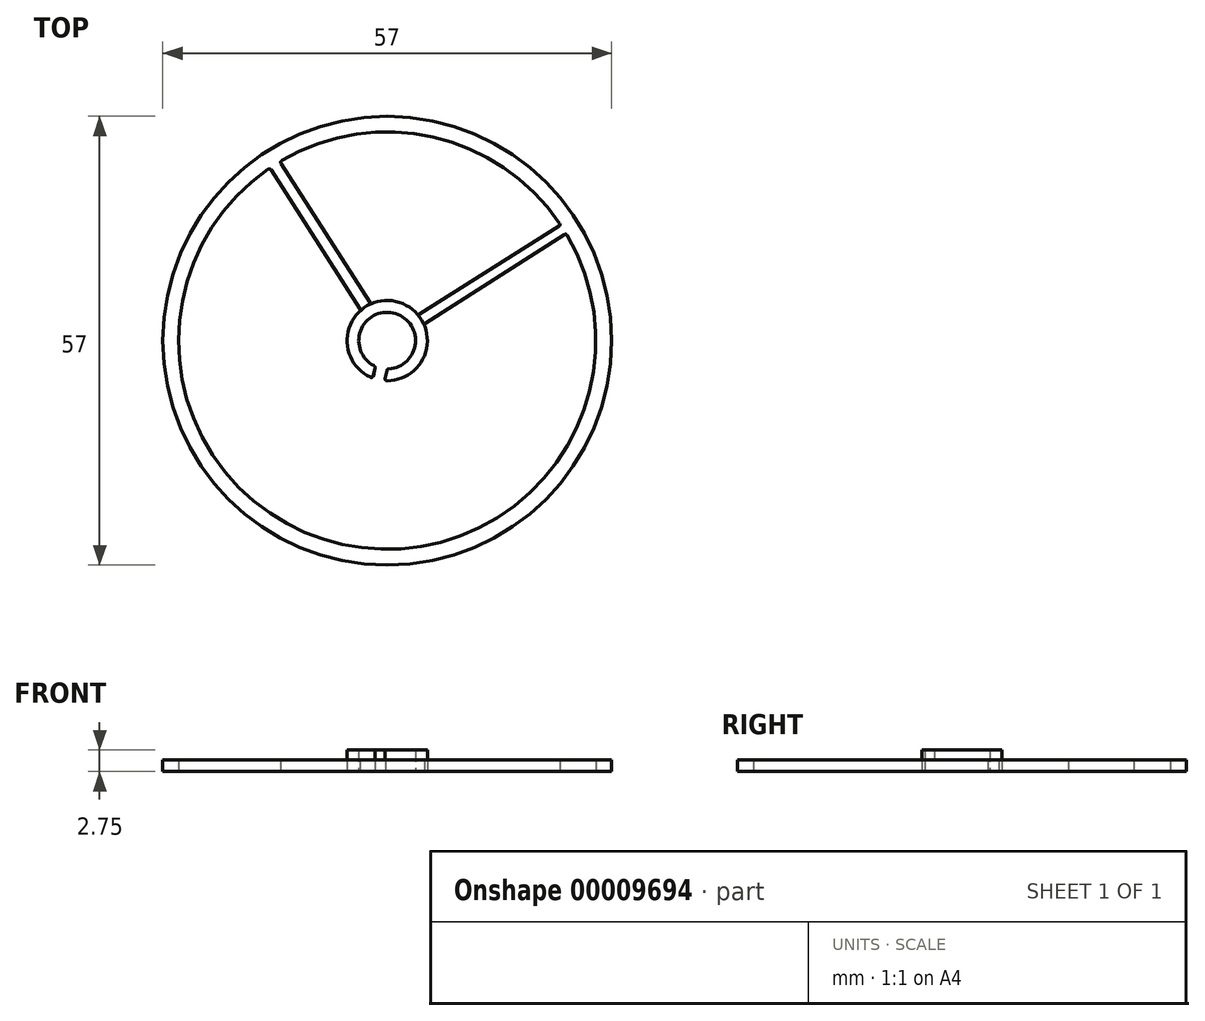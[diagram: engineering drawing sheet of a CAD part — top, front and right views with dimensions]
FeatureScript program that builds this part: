
annotation { "Feature Type Name" : "Feature", "Feature Type Description" : "" }
export const myFeature = defineFeature(function(context is Context, id is Id, definition is map)
    precondition{}
    {
        {
            var Q0;
            Q0=qCreatedBy(makeId("Top.planeOp"),FACE);
            var sketch = newSketch(context, id + "F0", { "sketchPlane" : qUnion([Q0])});
            skCircle(sketch, "E0", {"center": v(0, 0) * mm, "radius": 28.5 * mm});
            skArc(sketch, "E1.0", {"start": v(21.92, 14.89) * mm, "mid": v(5.84, 25.85) * mm, "end": v(-13.4, 22.87) * mm});
            skArc(sketch, "E2", {"start": v(0.2, -3.6) * mm, "mid": v(3.57, -0.47) * mm, "end": v(1.11, 3.42) * mm});
            skArc(sketch, "E3.0", {"start": v(3.8, 3.4) * mm, "mid": v(3.05, 4.08) * mm, "end": v(2.2, 4.6) * mm});
            skLineSegment(sketch, "E4.trimOffspring", {"start": v(4.12, 3.36) * mm, "end": v(21.85, 14.54) * mm});
            skLineSegment(sketch, "E5.trimOffspring", {"start": v(4.84, 2.18) * mm, "end": v(22.52, 13.48) * mm});
            skLineSegment(sketch, "E6.trimOffspring", {"start": v(-2.18, 4.84) * mm, "end": v(-13.48, 22.52) * mm});
            skLineSegment(sketch, "E7.trimOffspring", {"start": v(-3.47, 4.02) * mm, "end": v(-14.74, 21.7) * mm});
            skArc(sketch, "E8.trimOffspring", {"start": v(3.51, -3.7) * mm, "mid": v(4.98, -1.1) * mm, "end": v(4.74, 1.87) * mm});
            skArc(sketch, "E9.trimOffspring", {"start": v(-3.7, -3.51) * mm, "mid": v(-2.95, -4.16) * mm, "end": v(-2.1, -4.65) * mm});
            skArc(sketch, "E10.trimOffspring", {"start": v(-3.5, 3.7) * mm, "mid": v(-5.1, 0.14) * mm, "end": v(-3.7, -3.51) * mm});
            skArc(sketch, "E11.trimOffspring", {"start": v(13.41, -22.85) * mm, "mid": v(25.64, -6.69) * mm, "end": v(22.87, 13.4) * mm});
            skArc(sketch, "E12.trimOffspring", {"start": v(-22.87, -13.4) * mm, "mid": v(-6.69, -25.64) * mm, "end": v(13.41, -22.85) * mm});
            skArc(sketch, "E13.trimOffspring", {"start": v(-15.1, 21.78) * mm, "mid": v(-25.88, 5.72) * mm, "end": v(-22.87, -13.4) * mm});
            skLineSegment(sketch, "E14.0", {"start": v(-1.55, -3.45) * mm, "end": v(-1.75, -4.47) * mm});
            skLineSegment(sketch, "E15.0.MirrorCS", {"start": v(-0.04, -3.8) * mm, "end": v(-0.23, -4.8) * mm});
            skArc(sketch, "E16.trimOffspring", {"start": v(0.02, -5.1) * mm, "mid": v(1.9, -4.73) * mm, "end": v(3.51, -3.7) * mm});
            skArc(sketch, "E17.trimOffspring", {"start": v(1.11, 3.42) * mm, "mid": v(-3.32, 1.4) * mm, "end": v(-1.68, -3.18) * mm});
            skArc(sketch, "E18.trimOffspring", {"start": v(2.2, 4.6) * mm, "mid": v(0.17, 5.1) * mm, "end": v(-1.87, 4.74) * mm});
            skPoint(sketch, "E19.visualSharp", {"position": v(-1.52, -3.26) * mm});
            skArc(sketch, "E19.filletArc", {"start": v(-1.55, -3.45) * mm, "mid": v(-1.57, -3.3) * mm, "end": v(-1.68, -3.18) * mm});
            skPoint(sketch, "E20.visualSharp", {"position": v(-1.8, -4.77) * mm});
            skArc(sketch, "E20.filletArc", {"start": v(-2.1, -4.65) * mm, "mid": v(-1.88, -4.64) * mm, "end": v(-1.75, -4.47) * mm});
            skPoint(sketch, "E21.visualSharp", {"position": v(-0.29, -5.1) * mm});
            skArc(sketch, "E21.filletArc", {"start": v(-0.23, -4.8) * mm, "mid": v(-0.18, -5) * mm, "end": v(0.02, -5.1) * mm});
            skPoint(sketch, "E22.visualSharp", {"position": v(0, -3.6) * mm});
            skArc(sketch, "E22.filletArc", {"start": v(0.2, -3.6) * mm, "mid": v(0.04, -3.66) * mm, "end": v(-0.04, -3.8) * mm});
            skPoint(sketch, "E23.visualSharp", {"position": v(-3.35, 3.84) * mm});
            skArc(sketch, "E23.filletArc", {"start": v(-3.5, 3.7) * mm, "mid": v(-3.43, 3.86) * mm, "end": v(-3.47, 4.02) * mm});
            skPoint(sketch, "E24.visualSharp", {"position": v(-2.06, 4.66) * mm});
            skArc(sketch, "E24.filletArc", {"start": v(-2.18, 4.84) * mm, "mid": v(-2.04, 4.74) * mm, "end": v(-1.87, 4.74) * mm});
            skPoint(sketch, "E25.visualSharp", {"position": v(3.93, 3.24) * mm});
            skArc(sketch, "E25.filletArc", {"start": v(3.8, 3.4) * mm, "mid": v(3.95, 3.32) * mm, "end": v(4.12, 3.36) * mm});
            skPoint(sketch, "E26.visualSharp", {"position": v(4.66, 2.06) * mm});
            skArc(sketch, "E26.filletArc", {"start": v(4.84, 2.18) * mm, "mid": v(4.74, 2.04) * mm, "end": v(4.74, 1.87) * mm});
            skArc(sketch, "E27.filletArc", {"start": v(22.87, 13.4) * mm, "mid": v(22.7, 13.51) * mm, "end": v(22.52, 13.48) * mm});
            skPoint(sketch, "E28.visualSharp", {"position": v(22.07, 14.67) * mm});
            skArc(sketch, "E28.filletArc", {"start": v(21.85, 14.54) * mm, "mid": v(21.96, 14.7) * mm, "end": v(21.92, 14.89) * mm});
            skArc(sketch, "E29.filletArc", {"start": v(-13.4, 22.87) * mm, "mid": v(-13.51, 22.7) * mm, "end": v(-13.48, 22.52) * mm});
            skArc(sketch, "E30.filletArc", {"start": v(-14.74, 21.7) * mm, "mid": v(-14.9, 21.82) * mm, "end": v(-15.1, 21.78) * mm});
            skSolve(sketch);
        }
        {
            var Q0;
            Q0=qSketchRegion(id+"F0",true);
            extrude(context, id + "F1", {"entities" : qUnion([Q0]), "depth" : 1.5 * mm});
        }
        {
            var Q0;
            Q0=makeQuery(id+"F1.opExtrude","CAP_FACE",FACE,{"disambiguationData":[OSD([sQuery(id+"F0.wireOp",EDGE,"E0"),sQuery(id+"F0.wireOp",EDGE,"E1.0"),sQuery(id+"F0.wireOp",EDGE,"E2"),sQuery(id+"F0.wireOp",EDGE,"E3.0"),sQuery(id+"F0.wireOp",EDGE,"9aa386a5-fe43-4538-9e74-4b5fec4a8f2f.0"),sQuery(id+"F0.wireOp",EDGE,"af6841e1-3135-4da6-87f9-270789899b2d.0.MirrorCS"),sQuery(id+"F0.wireOp",EDGE,"af96ccba-543d-44e2-a15b-5b69eeccdc49.0"),sQuery(id+"F0.wireOp",EDGE,"de95141b-281c-47d2-a527-d31a5b29fca6.0.MirrorCS"),sQuery(id+"F0.wireOp",EDGE,"E4.trimOffspring"),sQuery(id+"F0.wireOp",EDGE,"E5.trimOffspring"),sQuery(id+"F0.wireOp",EDGE,"E6.trimOffspring"),sQuery(id+"F0.wireOp",EDGE,"E7.trimOffspring"),sQuery(id+"F0.wireOp",EDGE,"E8.trimOffspring"),sQuery(id+"F0.wireOp",EDGE,"E9.trimOffspring"),sQuery(id+"F0.wireOp",EDGE,"E10.trimOffspring"),sQuery(id+"F0.wireOp",EDGE,"E11.trimOffspring"),sQuery(id+"F0.wireOp",EDGE,"E12.trimOffspring"),sQuery(id+"F0.wireOp",EDGE,"E13.trimOffspring"),sQuery(id+"F0.wireOp",EDGE,"E14.0"),sQuery(id+"F0.wireOp",EDGE,"E15.0.MirrorCS"),sQuery(id+"F0.wireOp",EDGE,"E16.trimOffspring"),sQuery(id+"F0.wireOp",EDGE,"E17.trimOffspring"),sQuery(id+"F0.wireOp",EDGE,"E18.trimOffspring"),sQuery(id+"F0.wireOp",EDGE,"E19.filletArc"),sQuery(id+"F0.wireOp",EDGE,"E20.filletArc"),sQuery(id+"F0.wireOp",EDGE,"E21.filletArc"),sQuery(id+"F0.wireOp",EDGE,"E22.filletArc"),sQuery(id+"F0.wireOp",EDGE,"bd76ecdb-724b-4b7b-8fd4-4bbb9e199359.filletArc"),sQuery(id+"F0.wireOp",EDGE,"cc77ec8b-e015-4377-9976-1ebba4e718bb.filletArc"),sQuery(id+"F0.wireOp",EDGE,"E23.filletArc"),sQuery(id+"F0.wireOp",EDGE,"E24.filletArc"),sQuery(id+"F0.wireOp",EDGE,"E25.filletArc"),sQuery(id+"F0.wireOp",EDGE,"E26.filletArc"),sQuery(id+"F0.wireOp",EDGE,"d04b834a-b780-481d-b3f4-885520477cab.filletArc"),sQuery(id+"F0.wireOp",EDGE,"d3b0299a-e5d0-4b23-a270-884fe2cc609d.filletArc"),sQuery(id+"F0.wireOp",EDGE,"ff1316e2-f727-4fd1-9490-a6e8b23ddb40.filletArc"),sQuery(id+"F0.wireOp",EDGE,"eb0d2701-bcfa-4646-84e3-03c169fe0002.filletArc"),sQuery(id+"F0.wireOp",EDGE,"0ab88e22-3f51-4ce2-b02c-d742cf840d62.filletArc"),sQuery(id+"F0.wireOp",EDGE,"3afa36f0-d0f4-4050-ad42-3c3d691017ca.filletArc"),sQuery(id+"F0.wireOp",EDGE,"E27.filletArc"),sQuery(id+"F0.wireOp",EDGE,"E28.filletArc"),sQuery(id+"F0.wireOp",EDGE,"E29.filletArc"),sQuery(id+"F0.wireOp",EDGE,"E30.filletArc")])],"isStart":false});
            var sketch = newSketch(context, id + "F2", { "sketchPlane" : qUnion([Q0])});
            skArc(sketch, "E31", {"start": v(0.2, -3.6) * mm, "mid": v(3.57, -0.47) * mm, "end": v(1.11, 3.42) * mm});
            skArc(sketch, "E32.0", {"start": v(3.8, 3.4) * mm, "mid": v(3.05, 4.08) * mm, "end": v(2.2, 4.6) * mm});
            skArc(sketch, "E33.trimOffspring", {"start": v(1.89, -4.74) * mm, "mid": v(4.97, -1.16) * mm, "end": v(3.8, 3.4) * mm});
            skArc(sketch, "E34.trimOffspring", {"start": v(-4.7, -1.97) * mm, "mid": v(-3.66, -3.55) * mm, "end": v(-2.12, -4.64) * mm});
            skArc(sketch, "E35.trimOffspring", {"start": v(-3.5, 3.7) * mm, "mid": v(-4.99, 1.06) * mm, "end": v(-4.7, -1.97) * mm});
            skLineSegment(sketch, "E36.0", {"start": v(-1.55, -3.46) * mm, "end": v(-1.77, -4.46) * mm});
            skLineSegment(sketch, "E37.0.MirrorCS", {"start": v(-0.04, -3.8) * mm, "end": v(-0.25, -4.8) * mm});
            skArc(sketch, "E38.trimOffspring", {"start": v(0, -5.1) * mm, "mid": v(0.96, -5) * mm, "end": v(1.89, -4.74) * mm});
            skArc(sketch, "E39.trimOffspring", {"start": v(1.11, 3.42) * mm, "mid": v(-3.32, 1.4) * mm, "end": v(-1.68, -3.18) * mm});
            skArc(sketch, "E40.trimOffspring", {"start": v(2.2, 4.6) * mm, "mid": v(-0.8, 5.04) * mm, "end": v(-3.5, 3.7) * mm});
            skPoint(sketch, "E41.visualSharp", {"position": v(-1.51, -3.27) * mm});
            skArc(sketch, "E41.filletArc", {"start": v(-1.55, -3.46) * mm, "mid": v(-1.57, -3.3) * mm, "end": v(-1.68, -3.18) * mm});
            skPoint(sketch, "E42.visualSharp", {"position": v(-1.83, -4.76) * mm});
            skArc(sketch, "E42.filletArc", {"start": v(-2.12, -4.64) * mm, "mid": v(-1.9, -4.64) * mm, "end": v(-1.77, -4.46) * mm});
            skPoint(sketch, "E43.visualSharp", {"position": v(-0.31, -5.1) * mm});
            skArc(sketch, "E43.filletArc", {"start": v(-0.25, -4.8) * mm, "mid": v(-0.2, -5) * mm, "end": v(0, -5.1) * mm});
            skPoint(sketch, "E44.visualSharp", {"position": v(0, -3.6) * mm});
            skArc(sketch, "E44.filletArc", {"start": v(0.2, -3.6) * mm, "mid": v(0.05, -3.65) * mm, "end": v(-0.04, -3.8) * mm});
            skSolve(sketch);
        }
        {
            var Q0;
            Q0=qSketchRegion(id+"F2",true);
            extrude(context, id + "F3", {"entities" : qUnion([Q0]), "operationType" : NewBodyOperationType.ADD, "depth" : 1.25 * mm});
        }
    });
